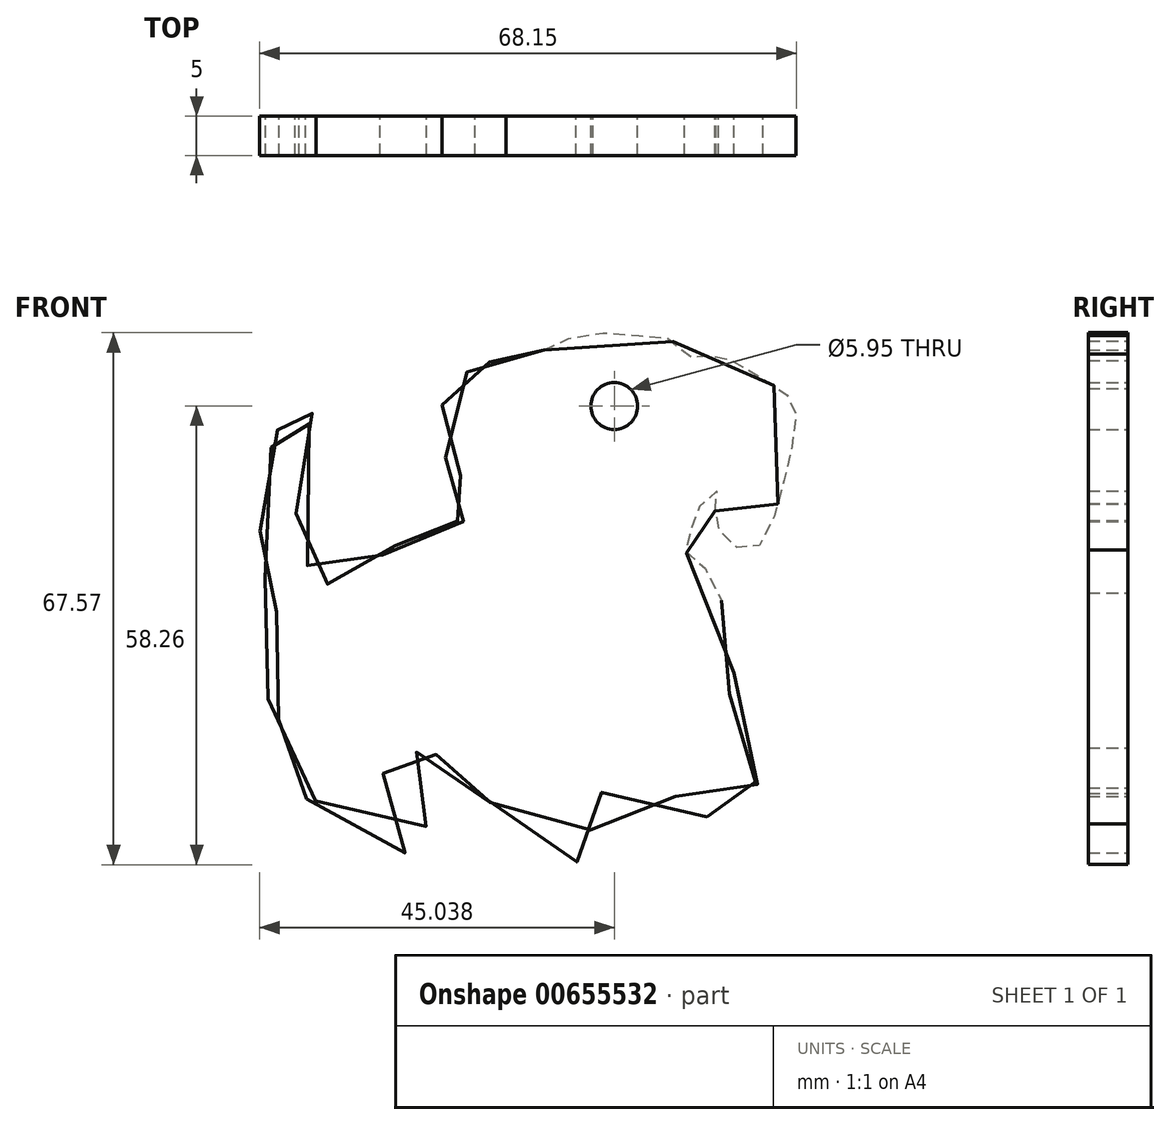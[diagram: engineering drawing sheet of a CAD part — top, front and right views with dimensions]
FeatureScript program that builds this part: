
annotation { "Feature Type Name" : "Feature", "Feature Type Description" : "" }
export const myFeature = defineFeature(function(context is Context, id is Id, definition is map)
    precondition{}
    {
        {
            var Q0;
            Q0=qCreatedBy(makeId("Front.planeOp"),FACE);
            var sketch = newSketch(context, id + "F0", { "sketchPlane" : qUnion([Q0])});
            skFitSpline(sketch, "E0", {"points": [v(4.77, 19.54) * mm, v(8.88, 21.4) * mm, v(16.17, 21.4) * mm, v(20.84, 20.84) * mm, v(24.4, 18.23) * mm, v(26.08, 18.97) * mm, v(29.26, 17.85) * mm, v(35.05, 14.3) * mm, v(36.73, 12.06) * mm, v(36.17, 6.82) * mm, v(34.5, 0) * mm, v(31.87, -5.51) * mm, v(28.88, -5.33) * mm, v(26.83, -2.9) * mm, v(26.64, 0) * mm, v(26.83, 1.59) * mm, v(24.77, 0) * mm, v(23.46, -3.27) * mm, v(22.71, -5.89) * mm, v(25.7, -8.7) * mm, v(28.13, -15.98) * mm, v(28.88, -20.66) * mm, v(28.5, -23.83) * mm, v(26.64, -28.5) * mm, v(30.2, -33.74) * mm, v(32.62, -37.3) * mm, v(30.94, -40.1) * mm, v(26.08, -40.1) * mm, v(20.84, -36.92) * mm, v(14.3, -37.1) * mm, v(8.88, -36.36) * mm, v(10.94, -43.65) * mm, v(4.77, -45.52) * mm, v(0, -40.66) * mm, v(-3.83, -35.8) * mm, v(-5.14, -34.12) * mm, v(-7.38, -32.8) * mm, v(-8.88, -31.87) * mm, v(-11.68, -31.5) * mm, v(-14.67, -31.13) * mm, v(-15.98, -33.56) * mm, v(-11.5, -38.23) * mm, v(-10.75, -43.65) * mm, v(-17.1, -43.09) * mm, v(-22.71, -38.23) * mm, v(-26.26, -36.92) * mm, v(-25.52, -33.37) * mm, v(-28.13, -28.5) * mm, v(-30.56, -22.53) * mm, v(-28.88, -15.24) * mm, v(-30.2, -11.68) * mm, v(-30.56, -9.81) * mm, v(-31.31, -4.77) * mm, v(-30.94, 0) * mm, v(-30.2, 5.89) * mm, v(-27.76, 11.87) * mm, v(-24.96, 14.67) * mm, v(-24.2, 13.74) * mm, v(-24.96, 10.56) * mm, v(-25.7, 7.38) * mm, v(-26.83, 0) * mm, v(-25.33, -7.57) * mm, v(-24.2, -11.3) * mm, v(-21.4, -9.07) * mm, v(-17.48, -7.94) * mm, v(-15.42, -6.26) * mm, v(-13.37, -4.95) * mm, v(-10.94, -3.65) * mm, v(-9.44, -2.71) * mm, v(-7.01, -2.15) * mm, v(-4.2, -1.78) * mm, v(-4.2, 0) * mm, v(-4.4, 0) * mm, v(-5.14, 2.34) * mm, v(-6.45, 4.2) * mm, v(-7.76, 5.89) * mm, v(-8.13, 10) * mm, v(-8.13, 13.18) * mm, v(-7.76, 14.49) * mm, v(-5.7, 16.17) * mm, v(-3.46, 17.67) * mm, v(0, 18.79) * mm, v(0, 19.72) * mm, v(1.96, 20.66) * mm, v(4.77, 19.54) * mm]});
            skCircle(sketch, "E1", {"center": v(13.7, 12.42) * mm, "radius": 2.97 * mm});
            skSolve(sketch);
        }
        {
            var Q0;
            Q0 = qSketchRegion(id + "F0", true);
            extrude(context, id + "F1", {"entities" : qUnion([Q0]), "depth" : 5 * mm, "offsetDistance" : 25.4 * mm});
        }
    });
